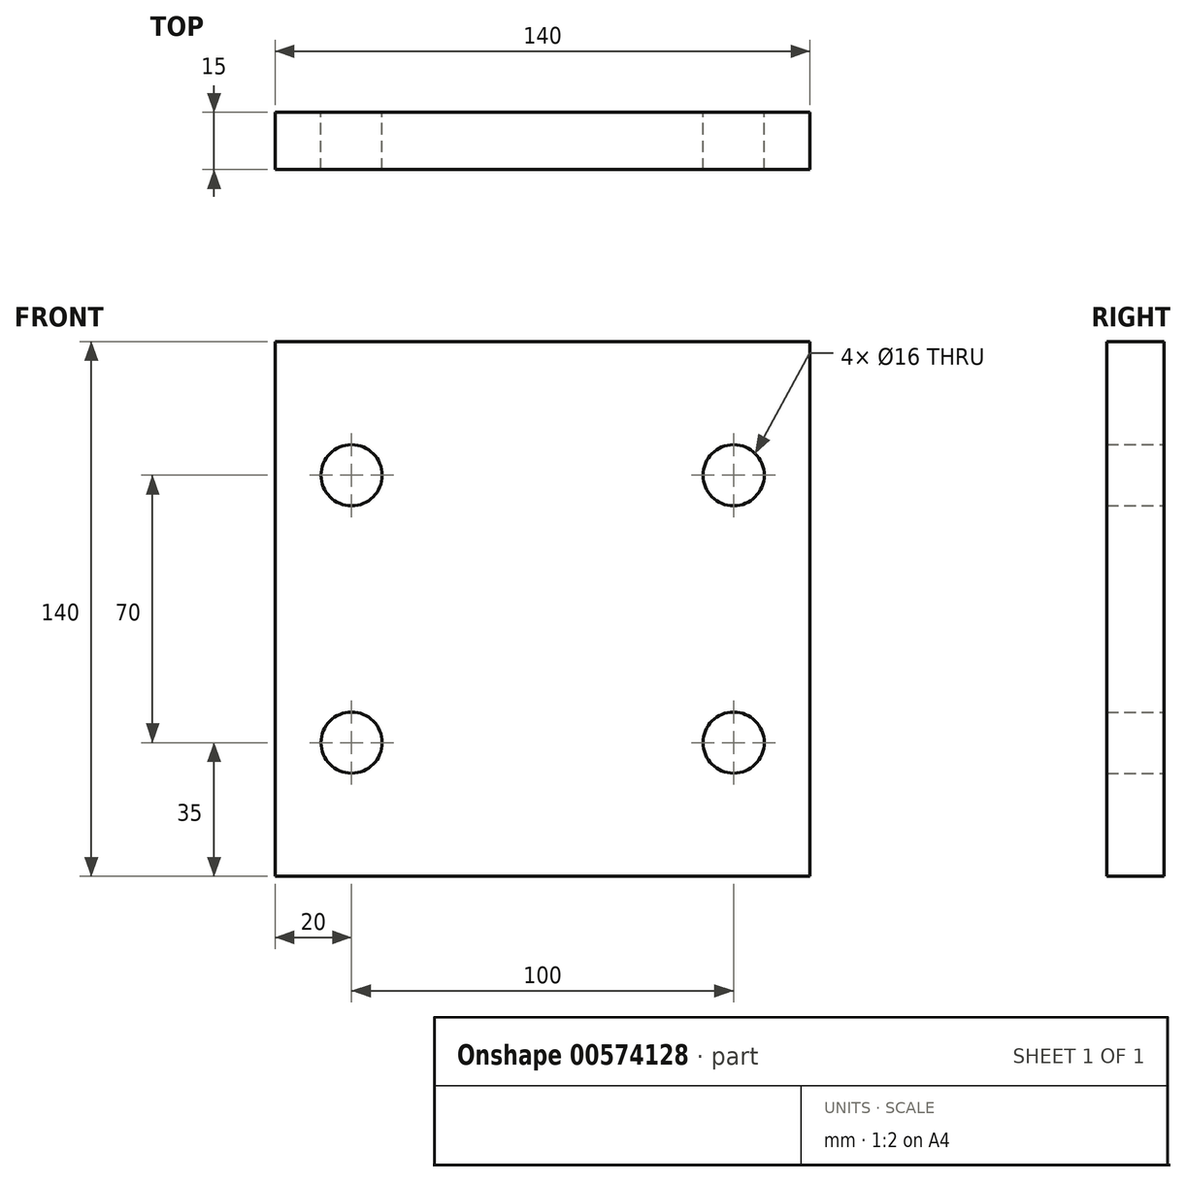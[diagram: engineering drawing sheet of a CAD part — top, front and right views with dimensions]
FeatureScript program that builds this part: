
annotation { "Feature Type Name" : "Feature", "Feature Type Description" : "" }
export const myFeature = defineFeature(function(context is Context, id is Id, definition is map)
    precondition{}
    {
        {
            var Q0;
            Q0=qCreatedBy(makeId("Front.planeOp"),FACE);
            var sketch = newSketch(context, id + "F0", { "sketchPlane" : qUnion([Q0])});
            skLineSegment(sketch, "E0.bottom", {"start": v(-70, 70) * mm, "end": v(70, 70) * mm});
            skLineSegment(sketch, "E0.top", {"start": v(-70, -70) * mm, "end": v(70, -70) * mm});
            skLineSegment(sketch, "E0.left", {"start": v(-70, 70) * mm, "end": v(-70, -70) * mm});
            skLineSegment(sketch, "E0.right", {"start": v(70, 70) * mm, "end": v(70, -70) * mm});
            skCircle(sketch, "E1", {"center": v(-50, 35) * mm, "radius": 8 * mm});
            skCircle(sketch, "E2", {"center": v(50, 35) * mm, "radius": 8 * mm});
            skCircle(sketch, "E3", {"center": v(-50, -35) * mm, "radius": 8 * mm});
            skCircle(sketch, "E4", {"center": v(50, -35) * mm, "radius": 8 * mm});
            skSolve(sketch);
        }
        {
            var Q0;
            Q0=makeQuery(id+"F0.imprint","IMPRINT",FACE,{"disambiguationData":[TD([[makeQuery(id+"F0.imprint","IMPRINT",EDGE,{"derivedFrom":sQuery(id+"F0.wireOp",EDGE,"E0.bottom")}),-1.0]])]});
            extrude(context, id + "F1", {"entities" : qUnion([Q0]), "depth" : 15 * mm, "offsetDistance" : 25 * mm});
        }
    });
